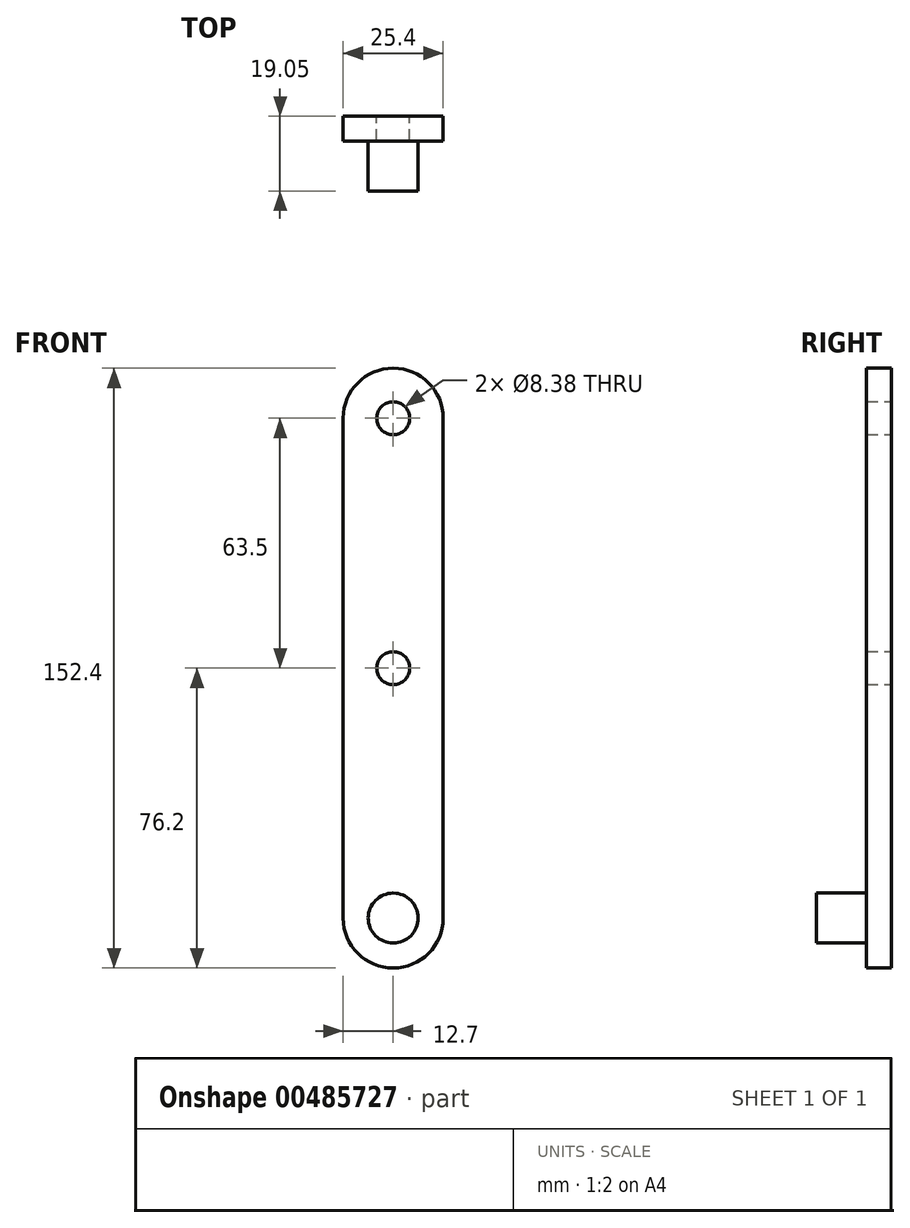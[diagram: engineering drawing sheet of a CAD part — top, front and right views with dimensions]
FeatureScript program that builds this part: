
annotation { "Feature Type Name" : "Feature", "Feature Type Description" : "" }
export const myFeature = defineFeature(function(context is Context, id is Id, definition is map)
    precondition{}
    {
        {
            var Q0;
            Q0=qCreatedBy(makeId("Front.planeOp"),FACE);
            var sketch = newSketch(context, id + "F0", { "sketchPlane" : qUnion([Q0])});
            skLineSegment(sketch, "E0.bottom", {"start": v(12.7, 63.5) * mm, "end": v(-12.7, 63.5) * mm});
            skLineSegment(sketch, "E0.top", {"start": v(12.7, -63.5) * mm, "end": v(-12.7, -63.5) * mm});
            skLineSegment(sketch, "E0.left", {"start": v(12.7, 63.5) * mm, "end": v(12.7, -63.5) * mm});
            skLineSegment(sketch, "E0.right", {"start": v(-12.7, 63.5) * mm, "end": v(-12.7, -63.5) * mm});
            skPoint(sketch, "E0.middle", {"position": v(0, 0) * mm});
            skPoint(sketch, "E1", {"position": v(0, 63.5) * mm});
            skPoint(sketch, "E2", {"position": v(0, -63.5) * mm});
            skCircle(sketch, "E3", {"center": v(0, -63.5) * mm, "radius": 12.7 * mm});
            skCircle(sketch, "E4", {"center": v(0, 63.5) * mm, "radius": 12.7 * mm});
            skCircle(sketch, "E5", {"center": v(0, -63.5) * mm, "radius": 6.35 * mm});
            skCircle(sketch, "E6", {"center": v(0, 0) * mm, "radius": 4.2 * mm});
            skCircle(sketch, "E7", {"center": v(0, 63.5) * mm, "radius": 4.2 * mm});
            skSolve(sketch);
        }
        {
            var Q0;
            {var subQ0=sQuery(id+"F0.wireOp",EDGE,"E0.bottom");Q0=makeQuery(id+"F0.imprint","IMPRINT",FACE,{"disambiguationData":[TD([[makeQuery(id+"F0.imprint","IMPRINT",EDGE,{"derivedFrom":subQ0}),-1.0]])]});}
            var Q1;
            {var subQ0=sQuery(id+"F0.wireOp",EDGE,"E0.bottom");Q1=makeQuery(id+"F0.imprint","IMPRINT",FACE,{"disambiguationData":[TD([[makeQuery(id+"F0.imprint","IMPRINT",EDGE,{"derivedFrom":subQ0}),1.0]])]});}
            var Q2;
            {var subQ1=sQuery(id+"F0.wireOp",EDGE,"E0.left");Q2=makeQuery(id+"F0.imprint","IMPRINT",FACE,{"disambiguationData":[TD([[makeQuery(id+"F0.imprint","IMPRINT",EDGE,{"derivedFrom":subQ1}),-1.0]])]});}
            var Q3;
            {var subQ1=sQuery(id+"F0.wireOp",EDGE,"E0.top");var subQ3=sQuery(id+"F0.wireOp",EDGE,"E5");var subQ4=makeQuery(id+"F0.imprint","INTERSECT",VERTEX,{"disambiguationData":[OD(0.0)],"derivedFrom":[subQ1,subQ3]});Q3=makeQuery(id+"F0.imprint","IMPRINT",FACE,{"disambiguationData":[TD([[makeQuery(id+"F0.imprint","IMPRINT",EDGE,{"disambiguationData":[TD([[subQ4,-1.0]])],"derivedFrom":subQ3}),-1.0]])]});}
            var Q4;
            {var subQ1=sQuery(id+"F0.wireOp",EDGE,"E0.top");var subQ3=sQuery(id+"F0.wireOp",EDGE,"E5");var subQ4=makeQuery(id+"F0.imprint","INTERSECT",VERTEX,{"disambiguationData":[OD(0.0)],"derivedFrom":[subQ1,subQ3]});Q4=makeQuery(id+"F0.imprint","IMPRINT",FACE,{"disambiguationData":[TD([[makeQuery(id+"F0.imprint","IMPRINT",EDGE,{"disambiguationData":[TD([[subQ4,1.0]])],"derivedFrom":subQ3}),-1.0]])]});}
            extrude(context, id + "F1", {"entities" : qUnion([Q0, Q1, Q2, Q3, Q4]), "depth" : 6.35 * mm});
        }
        {
            var Q0;
            {var subQ0=sQuery(id+"F0.wireOp",EDGE,"E5");var subQ1=sQuery(id+"F0.wireOp",EDGE,"E0.top");var subQ2=makeQuery(id+"F0.imprint","INTERSECT",VERTEX,{"disambiguationData":[OD(0.0)],"derivedFrom":[subQ1,subQ0]});Q0=makeQuery(id+"F0.imprint","IMPRINT",FACE,{"disambiguationData":[TD([[makeQuery(id+"F0.imprint","IMPRINT",EDGE,{"disambiguationData":[TD([[subQ2,-1.0]])],"derivedFrom":subQ1}),-1.0]])]});}
            var Q1;
            {var subQ0=sQuery(id+"F0.wireOp",EDGE,"E5");var subQ1=sQuery(id+"F0.wireOp",EDGE,"E0.top");var subQ2=makeQuery(id+"F0.imprint","INTERSECT",VERTEX,{"disambiguationData":[OD(0.0)],"derivedFrom":[subQ1,subQ0]});Q1=makeQuery(id+"F0.imprint","IMPRINT",FACE,{"disambiguationData":[TD([[makeQuery(id+"F0.imprint","IMPRINT",EDGE,{"disambiguationData":[TD([[subQ2,-1.0]])],"derivedFrom":subQ1}),1.0]])]});}
            extrude(context, id + "F2", {"entities" : qUnion([Q0, Q1]), "operationType" : NewBodyOperationType.ADD, "depth" : 19.05 * mm});
        }
    });
